# Revit family: Haworth_Patterns_Workwall_ArchitecturalDouble
name_source: partatom
category: Furniture Systems
revit_build: Autodesk Revit 2018 (Build: 20170223_1515(x64)
units: mm (PartAtom-declared; Revit-internal decimal feet)

## family parameters
Always vertical = Yes
Cut with Voids When Loaded = No
OmniClass Number = 23.40.70.14.64.21
OmniClass Title = Systems Furniture
Part Type = Normal
Room Calculation Point = No
Round Connector Dimension = Use Diameter
Shared = No
Work Plane-Based = No

## types (1)
- 78w 42d 76 1/2h
    # of Backer Panel = 2
    # of Shelves = 2
    2 in. Credenza Thickness = No
    Actual Credenza Height = 29 3/16"
    Actual Depth = 22"
    Actual Height = 76 1/2"
    Actual Inside Width = 72"
    Actual Suspended Shelf 1 Height = 8"
    Actual Width = 78"
    Assembly Code = E2020200
    Backer Finish = Haworth - Markerboard - White
    Backer Height = 48 1/2"
    Backer Width = 36"
    Credenza Height = 30"
    Credenza Top = No
    Credenza Top Finish = Haworth _ Wood _ White Oak
    Credenza Top Thickness = 1 3/16"
    Custom Size = No
    Description = Haworth - Patterns - Workwall - Architectural - Double
    Floor Support Shelf Door = Yes
    Floor Supported Shelf = Yes
    Floor Supported Shelf Finish = Haworth _ Wood _ White Oak
    Full Tackboard = Yes
    Height = 76 1/2"
    Manufacturer = Haworth
    Max # of Shelves = 2
    Max. Height = 92 1/2"
    Max. Width = 126"
    Min. Height = 44 1/2"
    Min. Width = 78"
    Model = Haworth - Patterns - Workwall - Architectural - Double
    Multi Sectional Backer = No
    Partial Tackboard = No
    Product Page URL = https://www.haworth.com
    Revision Number = 2
    Shelf Finish = Haworth _ Wood _ White Oak
    Shelf_1 = Yes
    Shelf_2 = Yes
    Shelf_3 = No
    Shell Thickness = 3"
    Size = Verify Final Dim. w/ Haworth
    Sliding Door Finish = Haworth _ Wood _ White Oak
    Stabalizer Panel Finish = Haworth _ Wood _ White Oak
    Stabilizer Height = 25"
    Standard Heights = 76 1/2, 92 1/2 in.
    Standard Widths = 78, 102, 126 in.
    Suspend Shelf Note = Suspended Shelf 1 is top shelf
    Suspended Shelf 1 Backer = No
    Suspended Shelf 1 Door = No
    Suspended Shelf 1 Height = 8"
    Suspended Shelf 2 Backer = No
    Suspended Shelf 2 Door = No
    Suspended Shelf 3 Backer = No
    Suspended Shelf 3 Door = No
    Sustainability Info = http://www.haworth.com
    Tackboard = No
    Tackboard Finish = Haworth _ Fabric _ Tellure _ Ivory 3A-35
    Tackboard Height = 24"
    URL = https://www.haworth.com
    Warranty = http://www.haworth.com
    Width = 78"
    Workwall Backer = Yes
    Workwall Shell Finish = Haworth _ Wood _ White Oak

## geometry (parser evidence)
native form markers: Blend x6, Sweep x33
no freeform markers — native parametric forms only
